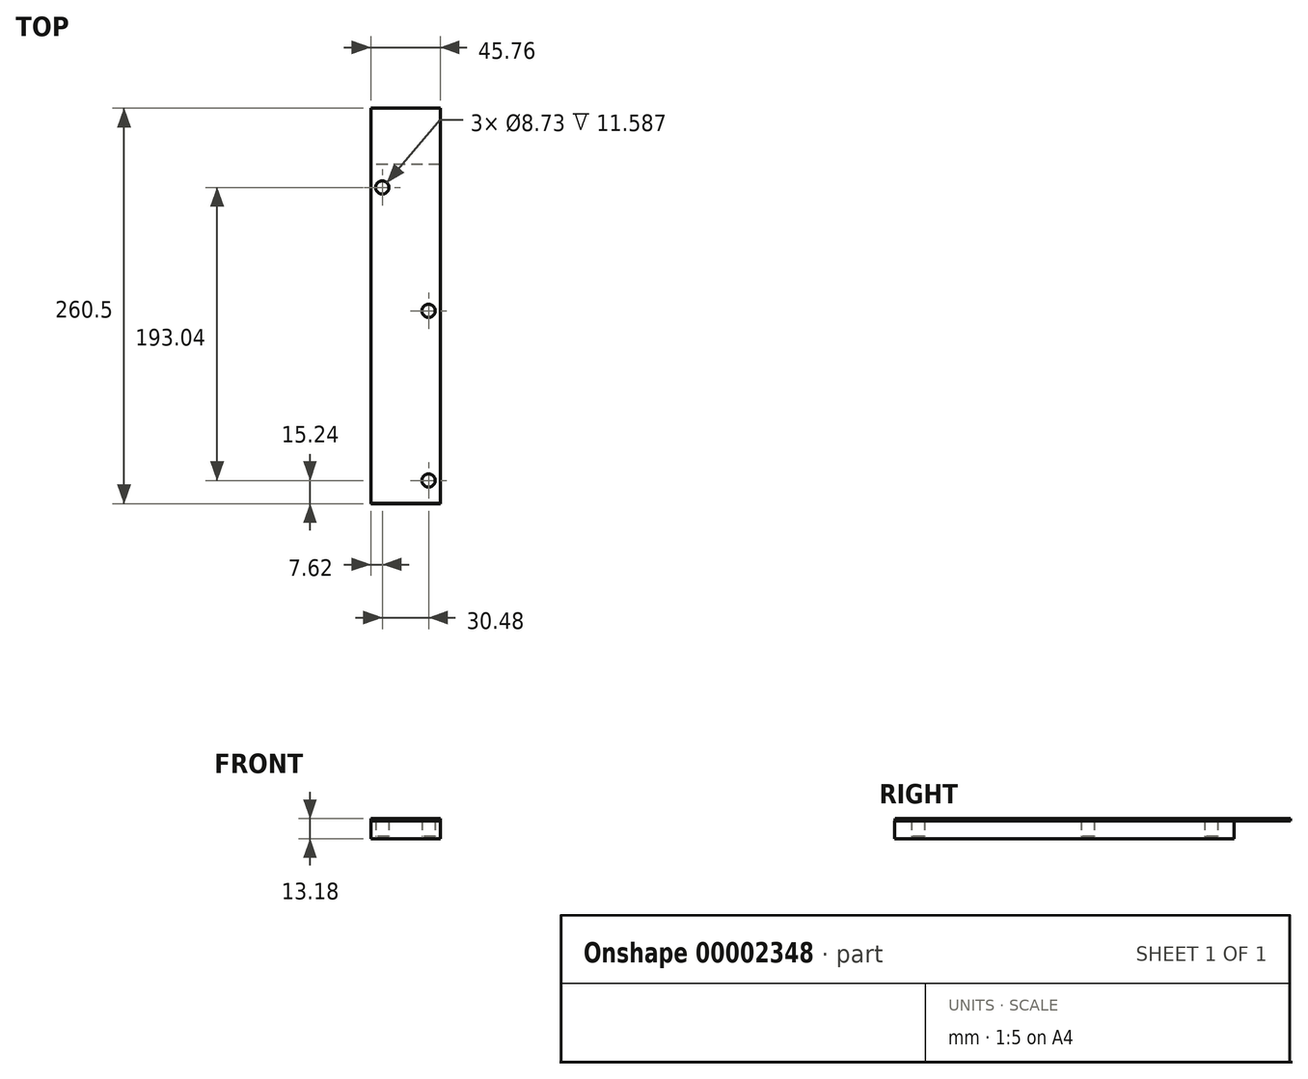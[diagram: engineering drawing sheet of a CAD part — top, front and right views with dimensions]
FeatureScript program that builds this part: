
annotation { "Feature Type Name" : "Feature", "Feature Type Description" : "" }
export const myFeature = defineFeature(function(context is Context, id is Id, definition is map)
    precondition{}
    {
        {
            var Q0;
            Q0=qCreatedBy(makeId("Top.planeOp"),FACE);
            var sketch = newSketch(context, id + "F0", { "sketchPlane" : qUnion([Q0])});
            skLineSegment(sketch, "E0.rect.bottom", {"start": v(22.86, 111.76) * mm, "end": v(-22.86, 111.76) * mm});
            skLineSegment(sketch, "E0.rect.top", {"start": v(22.86, -111.76) * mm, "end": v(-22.86, -111.76) * mm});
            skLineSegment(sketch, "E0.rect.left", {"start": v(22.86, 111.76) * mm, "end": v(22.86, -111.76) * mm});
            skLineSegment(sketch, "E0.rect.right", {"start": v(-22.86, 111.76) * mm, "end": v(-22.86, -111.76) * mm});
            skPoint(sketch, "E0.rect.middle", {"position": v(0, 0) * mm});
            skSolve(sketch);
        }
        {
            var Q0;
            Q0=makeQuery(id+"F0.imprint","IMPRINT",FACE,{"disambiguationData":[TD([[makeQuery(id+"F0.imprint","IMPRINT",EDGE,{"derivedFrom":sQuery(id+"F0.wireOp",EDGE,"E0.rect.bottom")}),1.0]])]});
            extrude(context, id + "F1", {"entities" : qUnion([Q0]), "depth" : 1.59 * mm});
        }
        {
            var Q0;
            Q0=makeQuery(id+"F1.opExtrude","CAP_FACE",FACE,{"disambiguationData":[OSD([sQuery(id+"F0.wireOp",EDGE,"E0.rect.bottom"),sQuery(id+"F0.wireOp",EDGE,"E0.rect.top"),sQuery(id+"F0.wireOp",EDGE,"E0.rect.left"),sQuery(id+"F0.wireOp",EDGE,"E0.rect.right")])],"isStart":false});
            var sketch = newSketch(context, id + "F2", { "sketchPlane" : qUnion([Q0])});
            skCircle(sketch, "E1.0.MirrorC", {"center": v(15.24, -96.52) * mm, "radius": 4.37 * mm});
            skCircle(sketch, "E2", {"center": v(15.24, 96.52) * mm, "radius": 4.37 * mm});
            skCircle(sketch, "E3.0.MirrorC", {"center": v(-15.24, -96.52) * mm, "radius": 4.37 * mm});
            skCircle(sketch, "E4.0.MirrorC", {"center": v(-15.24, 96.52) * mm, "radius": 4.37 * mm});
            skLineSegment(sketch, "E5", {"start": v(12.85, 0) * mm, "end": v(12.85, 55.88) * mm, "construction": true});
            skLineSegment(sketch, "E6", {"start": v(12.85, 55.88) * mm, "end": v(0, 55.88) * mm, "construction": true});
            skCircle(sketch, "E7.0.MirrorC", {"center": v(-15.24, 15.24) * mm, "radius": 4.37 * mm});
            skCircle(sketch, "E8.0.MirrorC", {"center": v(15.24, 15.24) * mm, "radius": 4.37 * mm});
            skSolve(sketch);
        }
        {
            var Q0;
            {Q0=qUnion([makeQuery(id+"F2.imprint","IMPRINT",FACE,{"disambiguationData":[TD([[makeQuery(id+"F2.imprint","IMPRINT",EDGE,{"derivedFrom":sQuery(id+"F2.wireOp",EDGE,"E1.0.MirrorC")}),-1.0]])]}),makeQuery(id+"F2.imprint","IMPRINT",FACE,{"disambiguationData":[TD([[makeQuery(id+"F2.imprint","IMPRINT",EDGE,{"derivedFrom":sQuery(id+"F2.wireOp",EDGE,"E2")}),1.0]])]}),makeQuery(id+"F2.imprint","IMPRINT",FACE,{"disambiguationData":[TD([[makeQuery(id+"F2.imprint","IMPRINT",EDGE,{"derivedFrom":sQuery(id+"F2.wireOp",EDGE,"E3.0.MirrorC")}),1.0]])]}),makeQuery(id+"F2.imprint","IMPRINT",FACE,{"disambiguationData":[TD([[makeQuery(id+"F2.imprint","IMPRINT",EDGE,{"derivedFrom":sQuery(id+"F2.wireOp",EDGE,"E4.0.MirrorC")}),-1.0]])]}),makeQuery(id+"F2.imprint","IMPRINT",FACE,{"disambiguationData":[TD([[makeQuery(id+"F2.imprint","IMPRINT",EDGE,{"derivedFrom":sQuery(id+"F2.wireOp",EDGE,"E7.0.MirrorC")}),1.0]])]}),makeQuery(id+"F2.imprint","IMPRINT",FACE,{"disambiguationData":[TD([[makeQuery(id+"F2.imprint","IMPRINT",EDGE,{"derivedFrom":sQuery(id+"F2.wireOp",EDGE,"E8.0.MirrorC")}),-1.0]])]})]);}
            extrude(context, id + "F3", {"entities" : qUnion([Q0]), "operationType" : NewBodyOperationType.ADD, "depth" : 10 * mm});
        }
        {
            var Q0;
            Q0=makeQuery(id+"F3.opExtrude","CAP_FACE",FACE,{"disambiguationData":[OSD([sQuery(id+"F2.wireOp",EDGE,"E4.0.MirrorC")])],"isStart":false});
            var sketch = newSketch(context, id + "F4", { "sketchPlane" : qUnion([Q0])});
            skLineSegment(sketch, "E9", {"start": v(-22.82, -111.61) * mm, "end": v(22.9, -111.61) * mm});
            skLineSegment(sketch, "E10", {"start": v(22.9, -111.61) * mm, "end": v(22.9, 148.74) * mm});
            skLineSegment(sketch, "E11", {"start": v(22.9, 148.74) * mm, "end": v(-22.73, 148.74) * mm});
            skLineSegment(sketch, "E12", {"start": v(-22.73, 148.74) * mm, "end": v(-22.82, -111.61) * mm});
            skSolve(sketch);
        }
        {
            var Q0;
            {var subQ0=makeQuery(id+"F4.imprint","IMPRINT",EDGE,{"derivedFrom":makeQuery(id+"F3.opExtrude","CAP_EDGE",EDGE,{"disambiguationData":[OSD([sQuery(id+"F2.wireOp",EDGE,"E4.0.MirrorC")])],"isStart":false})});Q0=qUnion([makeQuery(id+"F4.imprint","IMPRINT",FACE,{"disambiguationData":[TD([[makeQuery(id+"F4.imprint","IMPRINT",EDGE,{"derivedFrom":sQuery(id+"F4.wireOp",EDGE,"E9")}),1.0]])]}),makeQuery(id+"F4.imprint","IMPRINT",FACE,{"disambiguationData":[TD([[subQ0,-1.0]])]})]);}
            extrude(context, id + "F5", {"entities" : qUnion([Q0]), "operationType" : NewBodyOperationType.ADD, "depth" : 1.59 * mm});
        }
    });
